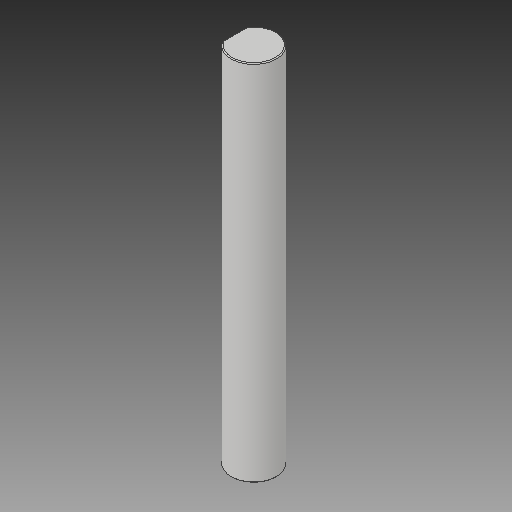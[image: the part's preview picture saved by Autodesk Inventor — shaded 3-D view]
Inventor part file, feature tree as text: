
AUTODESK INVENTOR PART (.ipt)
format: ipt  version: 2019 (Build 230136000, 136)  size: 85,504 bytes
history: native  units: in
note: dims shown in document units (in); Inventor stores cm internally (conversion verified against a paired STEP export)
features: chamfer x1
ambient origin geometry x8: Origin, YZ Plane, XZ Plane, XY Plane, X Axis, Y Axis, Z Axis, Center Point
bodies: Solid1 (feature_tree)
feature tree (1):
  chamfer  "Chamfer1"  [1 undecoded]
note: 1 required parameter value undecoded (feature->parameter linkage not recoverable at this tier; creation-order binding heuristic only, values carry confidence <= 0.55)
